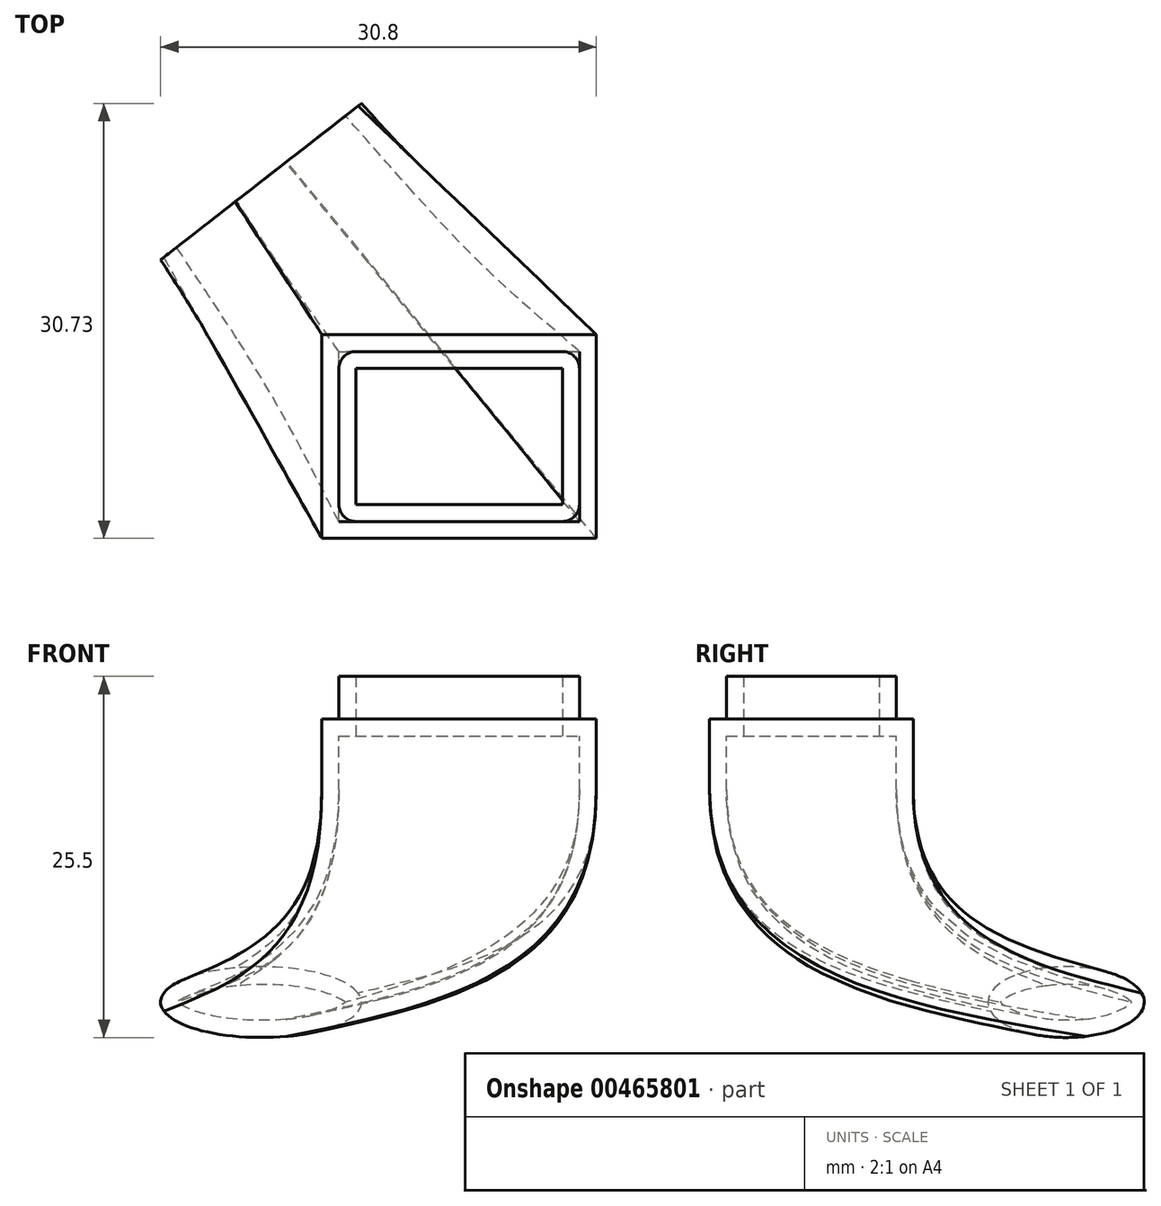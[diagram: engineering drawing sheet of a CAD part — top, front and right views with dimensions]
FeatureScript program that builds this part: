
annotation { "Feature Type Name" : "Feature", "Feature Type Description" : "" }
export const myFeature = defineFeature(function(context is Context, id is Id, definition is map)
    precondition{}
    {
        {
            var Q0;
            Q0=qCreatedBy(makeId("Top.planeOp"),FACE);
            var sketch = newSketch(context, id + "F0", { "sketchPlane" : qUnion([Q0])});
            skLineSegment(sketch, "E0.bottom", {"start": v(0, 0) * mm, "end": v(17, 0) * mm});
            skLineSegment(sketch, "E0.top", {"start": v(0, 12) * mm, "end": v(17, 12) * mm});
            skLineSegment(sketch, "E0.left", {"start": v(0, 0) * mm, "end": v(0, 12) * mm});
            skLineSegment(sketch, "E0.right", {"start": v(17, 0) * mm, "end": v(17, 12) * mm});
            skLineSegment(sketch, "E1.0", {"start": v(-1.2, 13.2) * mm, "end": v(18.2, 13.2) * mm});
            skLineSegment(sketch, "E1.1", {"start": v(-1.2, -1.2) * mm, "end": v(-1.2, 13.2) * mm});
            skLineSegment(sketch, "E1.2", {"start": v(-1.2, -1.2) * mm, "end": v(18.2, -1.2) * mm});
            skLineSegment(sketch, "E1.3", {"start": v(18.2, -1.2) * mm, "end": v(18.2, 13.2) * mm});
            skPoint(sketch, "E2", {"position": v(-5.5, 24) * mm});
            skLineSegment(sketch, "E3", {"start": v(0, 12) * mm, "end": v(17, 0) * mm, "construction": true});
            skLineSegment(sketch, "E4", {"start": v(17, 12) * mm, "end": v(0, 0) * mm, "construction": true});
            skPoint(sketch, "E5", {"position": v(8.5, 6) * mm});
            skLineSegment(sketch, "E6", {"start": v(-5.5, 24) * mm, "end": v(8.5, 6) * mm, "construction": true});
            skSolve(sketch);
        }
        {
            var Q0;
            Q0=makeQuery(id+"F0.imprint","IMPRINT",FACE,{"disambiguationData":[TD([[makeQuery(id+"F0.imprint","IMPRINT",EDGE,{"derivedFrom":sQuery(id+"F0.wireOp",EDGE,"E0.bottom")}),1.0]])]});
            extrude(context, id + "F1", {"entities" : qUnion([Q0]), "depth" : 3 * mm});
        }
        {
            var Q0;
            Q0=makeQuery(id+"F0.imprint","IMPRINT",FACE,{"disambiguationData":[TD([[makeQuery(id+"F0.imprint","IMPRINT",EDGE,{"derivedFrom":sQuery(id+"F0.wireOp",EDGE,"E0.bottom")}),1.0]])]});
            var Q1;
            Q1=makeQuery(id+"F0.imprint","IMPRINT",FACE,{"disambiguationData":[TD([[makeQuery(id+"F0.imprint","IMPRINT",EDGE,{"derivedFrom":sQuery(id+"F0.wireOp",EDGE,"E0.bottom")}),-1.0]])]});
            extrude(context, id + "F2", {"entities" : qUnion([Q0, Q1]), "operationType" : NewBodyOperationType.ADD, "oppositeDirection" : true, "depth" : 5 * mm});
        }
        {
            var Q0;
            Q0=sQuery(id+"F0.wireOp",VERTEX,"E2");
            var Q1;
            Q1=sQuery(id+"F0.wireOp",EDGE,"E6");
            cPlane(context, id + "F3", {"entities" : qUnion([Q0, Q1]), "cplaneType" : CPlaneType.LINE_POINT, "offset" : 25 * mm, "width" : 150 * mm, "height" : 150 * mm});
        }
        {
            var Q0;
            Q0=qCreatedBy(id+"F3.planeOp",FACE);
            var sketch = newSketch(context, id + "F4", { "sketchPlane" : qUnion([Q0])});
            skPoint(sketch, "E7.0", {"position": v(10.4, 0) * mm});
            skLineSegment(sketch, "E8", {"start": v(10.4, 0) * mm, "end": v(10.4, -20) * mm, "construction": true});
            skEllipse(sketch, "E9", {"center": v(10.4, -20) * mm, "majorRadius": 9 * mm, "minorRadius": 2.5 * mm, "majorAxis": v(1, 0)});
            skSolve(sketch);
        }
        {
            var Q1;
            Q1=makeQuery(id+"F2.opExtrude","CAP_FACE",FACE,{"disambiguationData":[OSD([sQuery(id+"F0.wireOp",EDGE,"E1.0"),sQuery(id+"F0.wireOp",EDGE,"E1.1"),sQuery(id+"F0.wireOp",EDGE,"E1.2"),sQuery(id+"F0.wireOp",EDGE,"E1.3")])],"isStart":false});
            var Q2;
            Q2=makeQuery(id+"F4.imprint","IMPRINT",FACE,{"disambiguationData":[TD([[makeQuery(id+"F4.imprint","IMPRINT",EDGE,{"derivedFrom":sQuery(id+"F4.wireOp",EDGE,"E9")}),1.0]])]});
            loft(context, id + "F5", {"operationType" : NewBodyOperationType.ADD, "startCondition" : LoftEndDerivativeType.NORMAL_TO_PROFILE, "startMagnitude" : 2, "sheetProfilesArray" : [{ "sheetProfileEntities" : qUnion([Q1]) }, { "sheetProfileEntities" : qUnion([Q2]) }]});
        }
        {
            var Q0;
            Q0=makeQuery(id+"F5.opLoft","CAP_FACE",FACE,{"disambiguationData":[OSD([makeQuery(id+"F4.imprint","IMPRINT",FACE,{"disambiguationData":[TD([[makeQuery(id+"F4.imprint","IMPRINT",EDGE,{"derivedFrom":sQuery(id+"F4.wireOp",EDGE,"E9")}),1.0]])]})])],"isStart":true});
            var Q1;
            Q1=makeQuery(id+"F1.opExtrude","CAP_FACE",FACE,{"disambiguationData":[OSD([sQuery(id+"F0.wireOp",EDGE,"E0.bottom"),sQuery(id+"F0.wireOp",EDGE,"E0.top"),sQuery(id+"F0.wireOp",EDGE,"E0.left"),sQuery(id+"F0.wireOp",EDGE,"E0.right")])],"isStart":false});
            shell(context, id + "F6", {"entities" : qUnion([Q0, Q1]), "thickness" : 1.2 * mm});
        }
        {
            var Q0;
            Q0=makeQuery(id+"F1.opExtrude","SWEPT_EDGE",EDGE,{"disambiguationData":[OSD([sQuery(id+"F0.wireOp",EDGE,"E0.top"),sQuery(id+"F0.wireOp",EDGE,"E0.right")])]});
            var Q1;
            Q1=makeQuery(id+"F1.opExtrude","SWEPT_EDGE",EDGE,{"disambiguationData":[OSD([sQuery(id+"F0.wireOp",EDGE,"E0.top"),sQuery(id+"F0.wireOp",EDGE,"E0.left")])]});
            var Q2;
            Q2=makeQuery(id+"F1.opExtrude","SWEPT_EDGE",EDGE,{"disambiguationData":[OSD([sQuery(id+"F0.wireOp",EDGE,"E0.bottom"),sQuery(id+"F0.wireOp",EDGE,"E0.right")])]});
            var Q3;
            Q3=makeQuery(id+"F1.opExtrude","SWEPT_EDGE",EDGE,{"disambiguationData":[OSD([sQuery(id+"F0.wireOp",EDGE,"E0.bottom"),sQuery(id+"F0.wireOp",EDGE,"E0.left")])]});
            fillet(context, id + "F7", {"entities" : qUnion([Q0, Q1, Q2, Q3]), "radius" : 1.2 * mm, "tangentPropagation" : true, "allowEdgeOverflow" : false});
        }
    });
